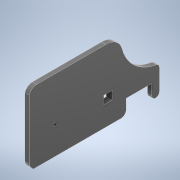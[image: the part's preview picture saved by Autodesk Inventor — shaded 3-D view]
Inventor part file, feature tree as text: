
AUTODESK INVENTOR PART (.ipt)
format: ipt  version: 2022 (Build 260153000, 153)  size: 511,488 bytes
history: native  units: in
note: dims shown in document units (in); Inventor stores cm internally (conversion verified against a paired STEP export)
features: extrude x6, other x5, sketch x4, mirror x1
ambient origin geometry x8: Origin, YZ Plane, XZ Plane, XY Plane, X Axis, Y Axis, Z Axis, Center Point
bodies: Solid1 (feature_tree)
feature tree (16):
  other  "outline"
  extrude  "main right panel"  Depth=5.0in
  other  "rat icon raw"
  extrude  "the rat boys words"  Depth=1.75in
  extrude  "car details extrusion"  Depth=0.25in
  extrude  "rat extrusion"  Depth=0.5in
  mirror  "Mirror1"
  extrude  "rat boys ketters"  Depth=0.5in
  extrude  "arduino plug hole"  Depth=0.5in
  sketch  "Sketch2"  dims[d0=7.0in d1=5.0in]
  other  "detail lines"
  other  "Image1"
  other  "rat sketch"
  sketch  "Sketch6"  dims[d2=1.5in d3=1.75in]
  sketch  "Sketch7"  dims[d4=0.25in d5=0.25in]
  sketch  "Sketch8"  dims[d6=0.25in d7=0.25in d8=0.1875in d9=0.972in d10=5.878in d11=0.25in d12=0.0in d44=0.2in d45=0.0in d46=0.1in d47=0.0in d48=0.25in d49=0.0in d50=0.25in d51=0.0in d52=0.8in d53=0.3in d54=0.5in d55=0.5in d56=0.4375in d57=0.0in]
